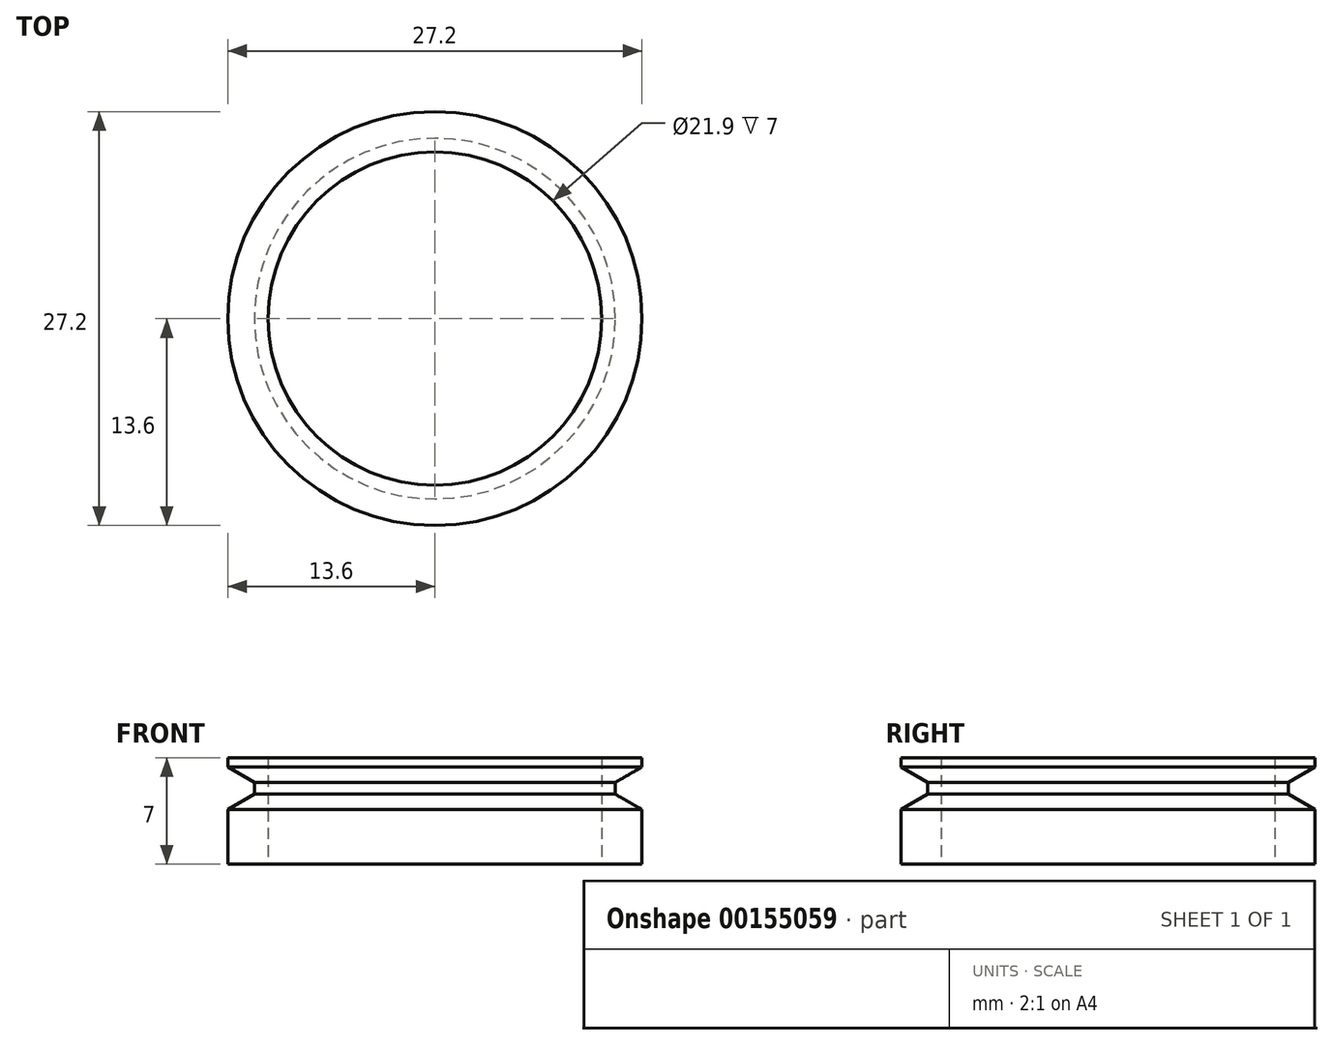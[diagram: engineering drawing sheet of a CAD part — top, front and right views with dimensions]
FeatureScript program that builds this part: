
annotation { "Feature Type Name" : "Feature", "Feature Type Description" : "" }
export const myFeature = defineFeature(function(context is Context, id is Id, definition is map)
    precondition{}
    {
        {
            var Q0;
            Q0=qCreatedBy(makeId("Top.planeOp"),FACE);
            var sketch = newSketch(context, id + "F0", { "sketchPlane" : qUnion([Q0])});
            skCircle(sketch, "E0", {"center": v(0, 0) * mm, "radius": 10.95 * mm});
            skCircle(sketch, "E1", {"center": v(0, 0) * mm, "radius": 13.6 * mm});
            skSolve(sketch);
        }
        {
            var Q0;
            Q0 = qSketchRegion(id + "F0", true);
            extrude(context, id + "F1", {"entities" : qUnion([Q0]), "depth" : 7 * mm});
        }
        {
            var Q0;
            Q0=qCreatedBy(makeId("Front.planeOp"),FACE);
            var sketch = newSketch(context, id + "F2", { "sketchPlane" : qUnion([Q0])});
            skPoint(sketch, "E2", {"position": v(44.43, 54.9) * mm});
            skLineSegment(sketch, "E3", {"start": v(13.6, 6.39) * mm, "end": v(13.6, 3.6) * mm});
            skLineSegment(sketch, "E4", {"start": v(13.6, 6.39) * mm, "end": v(13.6, 3.6) * mm, "construction": true});
            skPoint(sketch, "E5", {"position": v(13.6, 4.99) * mm});
            skLineSegment(sketch, "E6", {"start": v(13.6, 6.39) * mm, "end": v(11.85, 5.38) * mm});
            skLineSegment(sketch, "E7", {"start": v(11.85, 5.38) * mm, "end": v(11.85, 4.6) * mm});
            skLineSegment(sketch, "E8", {"start": v(11.85, 4.6) * mm, "end": v(13.6, 3.6) * mm});
            skLineSegment(sketch, "E9", {"start": v(13.6, 3.6) * mm, "end": v(13.6, 6.39) * mm});
            skPoint(sketch, "E10", {"position": v(11.85, 5) * mm});
            skLineSegment(sketch, "E11", {"start": v(13.6, 7) * mm, "end": v(13.6, 2.98) * mm, "construction": true});
            skPoint(sketch, "E12", {"position": v(13.6, 5) * mm});
            skLineSegment(sketch, "E13.0", {"start": v(-13.6, 7) * mm, "end": v(13.6, 7) * mm, "construction": true});
            skSolve(sketch);
        }
        {
            var Q0;
            Q0=makeQuery(id+"F2.imprint","IMPRINT",FACE,{"disambiguationData":[TD([[makeQuery(id+"F2.imprint","IMPRINT",EDGE,{"derivedFrom":sQuery(id+"F2.wireOp",EDGE,"E6")}),1.0]])]});
            var Q1;
            Q1=makeQuery(id+"F1.opExtrude","CAP_EDGE",EDGE,{"disambiguationData":[OSD([sQuery(id+"F0.wireOp",EDGE,"E0")])],"isStart":false});
            revolve(context, id + "F3", {"operationType" : NewBodyOperationType.REMOVE, "entities" : qUnion([Q0]), "axis" : qUnion([Q1]), "revolveType" : RevolveType.FULL, "oppositeDirection" : true});
        }
    });
